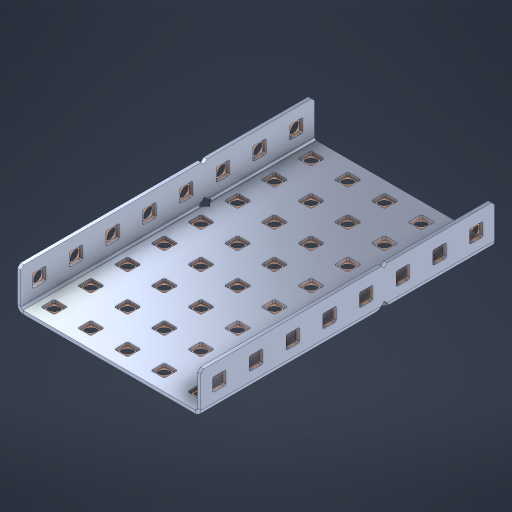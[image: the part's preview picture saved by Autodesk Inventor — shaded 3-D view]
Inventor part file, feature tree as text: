
AUTODESK INVENTOR PART (.ipt)
format: ipt  version: 2023 (Build 270158000, 158)  size: 911,360 bytes
history: native  units: in
note: dims shown in document units (in); Inventor stores cm internally (conversion verified against a paired STEP export)
features: other x61, extrude x55, sheet_metal_op x10, sketch x8, mirror x1, pattern_linear x1, chamfer x1
ambient origin geometry x8: Origin, YZ Plane, XZ Plane, XY Plane, X Axis, Y Axis, Z Axis, Center Point
bodies: Solid1 (feature_tree), Body (feature_tree)
feature tree (137):
  other  "Flange Pattern Plane"
  sheet_metal_op  "Flange Pattern"
  sheet_metal_op  "Body Pattern"
  other  "Arc Length"
  mirror  "Notch Mirror"
  pattern_linear  "Notch Pattern"  Spacing1=0.1875in  [1 undecoded]
  chamfer  "End Chamfer"
  extrude  "Half Cut"  Depth=0.0469in
  sketch  "Sketch1"  dims[d0=2.5in]
  other  "Plate1"
  sketch  "Sketch2"  dims[d1=4.0in]
  other  "Plate2"
  sheet_metal_op  "Bend1"
  sheet_metal_op  "Corner1"
  sketch  "Sketch3"  dims[d2=0.0469in]
  other  "Flange Pattern Sketch"
  sketch  "Sketch7"  dims[d3=0.0469in]
  other  "Srf1"
  other  "Srf2"
  sketch  "Sketch8"  dims[d4=0.0234in]
  sketch  "Sketch9"  dims[d5=0.0938in]
  other  "Srf91"
  sheet_metal_op  "Body Pattern Sketch"
  other  "Srf92"
  sketch  "Sketch13"  dims[d6=0.0469in]
  sketch  "Sketch14"  dims[d7=0.5in d8=90.0deg d9=0.0312in d10=0.1875in d11=0.0469in d12=0.0469in d16=0.182in d17=0.02in d18=0.0469in d19=0.0in d20=0.25in d21=0.25in d46=0.172in d47=1.0in d48=0.0in d49=0.182in d50=0.02in d51=0.25in d52=0.25in d53=0.0469in d54=0.0in d55=0.172in d56=1.0in d57=0.0in d60=3.1496in d62=0.5in d63=1.9685in d65=0.5in d85=0.1227in d86=0.1659in d88=0.04in d89=0.0469in d90=0.0in d91=0.04in d92=0.0491in d95=2.5in d96=0.04in d97=0.25in d98=45.0deg d101=0.0in d102=2.497in d131=2.5in d132=3.1496in d134=0.5in d139=0.5in]
  other  "Srf856"
  other  "Srf1310"
  other  "Srf1311"
  other  "Srf1312"
  other  "Srf1376"
  other  "Srf1377"
  other  "Srf1728"
  other  "Srf1755"
  other  "Srf1878"
  other  "Srf1879"
  other  "Srf1880"
  other  "Srf1881"
  other  "Srf1882"
  other  "Srf1883"
  other  "Srf1884"
  other  "Srf1885"
  other  "Srf1886"
  other  "Srf1887"
  other  "Srf1942"
  other  "Srf1943"
  other  "Srf1944"
  other  "Srf1945"
  other  "Srf1946"
  other  "Srf1947"
  other  "Srf1948"
  other  "Srf1949"
  other  "Srf1950"
  other  "Srf1951"
  other  "Srf1952"
  other  "Srf1953"
  other  "Srf1954"
  other  "Srf1955"
  other  "Srf1956"
  other  "Srf1957"
  other  "Srf1958"
  other  "Srf1959"
  other  "Srf1960"
  other  "Srf1961"
  other  "Srf1962"
  other  "Srf1963"
  other  "Srf1964"
  other  "Srf1965"
  other  "Srf1966"
  other  "Srf1967"
  other  "Srf1968"
  other  "Srf1969"
  other  "Srf1970"
  other  "Srf2146"
  other  "Srf2147"
  other  "Srf2148"
  other  "Srf2149"
  other  "Srf2150"
  sheet_metal_op  "Flange Stamp"
  sheet_metal_op  "Flange Circle"
  sheet_metal_op  "Body Stamp"
  sheet_metal_op  "Body Circle"
  sheet_metal_op  "Notch"
  extrude  "ExtrusionSrf2"  Depth=0.0469in
  extrude  "ExtrusionSrf92"  Depth=2.5in
  extrude  "ExtrusionSrf856"  Depth=0.02in
  extrude  "ExtrusionSrf1310"  Depth=0.0469in
  extrude  "ExtrusionSrf1311"  TaperAngle=0.0deg  [1 undecoded]
  extrude  "ExtrusionSrf1312"  Depth=0.25in
  extrude  "ExtrusionSrf1376"  Depth=0.25in
  extrude  "ExtrusionSrf1377"  Depth=2.5in
  extrude  "ExtrusionSrf1728"  Depth=2.5in TaperAngle=0.0deg
  extrude  "ExtrusionSrf1755"  Depth=2.5in
  extrude  "ExtrusionSrf1878"  Depth=0.02in
  extrude  "ExtrusionSrf1879"  Depth=0.25in
  extrude  "ExtrusionSrf1880"  Depth=0.25in
  extrude  "ExtrusionSrf1881"  Depth=0.0469in
  extrude  "ExtrusionSrf1882"  TaperAngle=0.0deg  [1 undecoded]
  extrude  "ExtrusionSrf1883"  Depth=2.5in
  extrude  "ExtrusionSrf1884"  Depth=2.5in TaperAngle=0.0deg
  extrude  "ExtrusionSrf1885"  Depth=2.5in
  extrude  "ExtrusionSrf1886"  Depth=2.5in
  extrude  "ExtrusionSrf1887"  Depth=2.5in
  extrude  "ExtrusionSrf1942"  Depth=2.5in
  extrude  "ExtrusionSrf1943"  Depth=2.5in
  extrude  "ExtrusionSrf1944"  Depth=0.0469in
  extrude  "ExtrusionSrf1945"  TaperAngle=0.0deg  [1 undecoded]
  extrude  "ExtrusionSrf1946"  Depth=2.5in
  extrude  "ExtrusionSrf1947"  Depth=2.5in
  extrude  "ExtrusionSrf1948"  Depth=2.5in
  extrude  "ExtrusionSrf1949"  Depth=0.25in TaperAngle=45.0deg
  extrude  "ExtrusionSrf1950"  TaperAngle=0.0deg  [1 undecoded]
  extrude  "ExtrusionSrf1951"  Depth=2.5in
  extrude  "ExtrusionSrf1952"  Depth=2.5in
  extrude  "ExtrusionSrf1953"  Depth=2.5in
  extrude  "ExtrusionSrf1954"  Depth=2.5in
  extrude  "ExtrusionSrf1955"  Depth=2.5in
  extrude  "ExtrusionSrf1956"  [1 undecoded]
  extrude  "ExtrusionSrf1957"  [1 undecoded]
  extrude  "ExtrusionSrf1958"  [1 undecoded]
  extrude  "ExtrusionSrf1959"  [1 undecoded]
  extrude  "ExtrusionSrf1960"  [1 undecoded]
  extrude  "ExtrusionSrf1961"  [1 undecoded]
  extrude  "ExtrusionSrf1962"  [1 undecoded]
  extrude  "ExtrusionSrf1963"  [1 undecoded]
  extrude  "ExtrusionSrf1964"  [1 undecoded]
  extrude  "ExtrusionSrf1965"  [1 undecoded]
  extrude  "ExtrusionSrf1966"  [1 undecoded]
  extrude  "ExtrusionSrf1967"  [1 undecoded]
  extrude  "ExtrusionSrf1968"  [1 undecoded]
  extrude  "ExtrusionSrf1969"  [1 undecoded]
  extrude  "ExtrusionSrf1970"  [1 undecoded]
  extrude  "ExtrusionSrf2146"  [1 undecoded]
  extrude  "ExtrusionSrf2147"  [1 undecoded]
  extrude  "ExtrusionSrf2148"  [1 undecoded]
  extrude  "ExtrusionSrf2149"  [1 undecoded]
  extrude  "ExtrusionSrf2150"  [1 undecoded]
note: 25 required parameter values undecoded (feature->parameter linkage not recoverable at this tier; creation-order binding heuristic only, values carry confidence <= 0.55)
